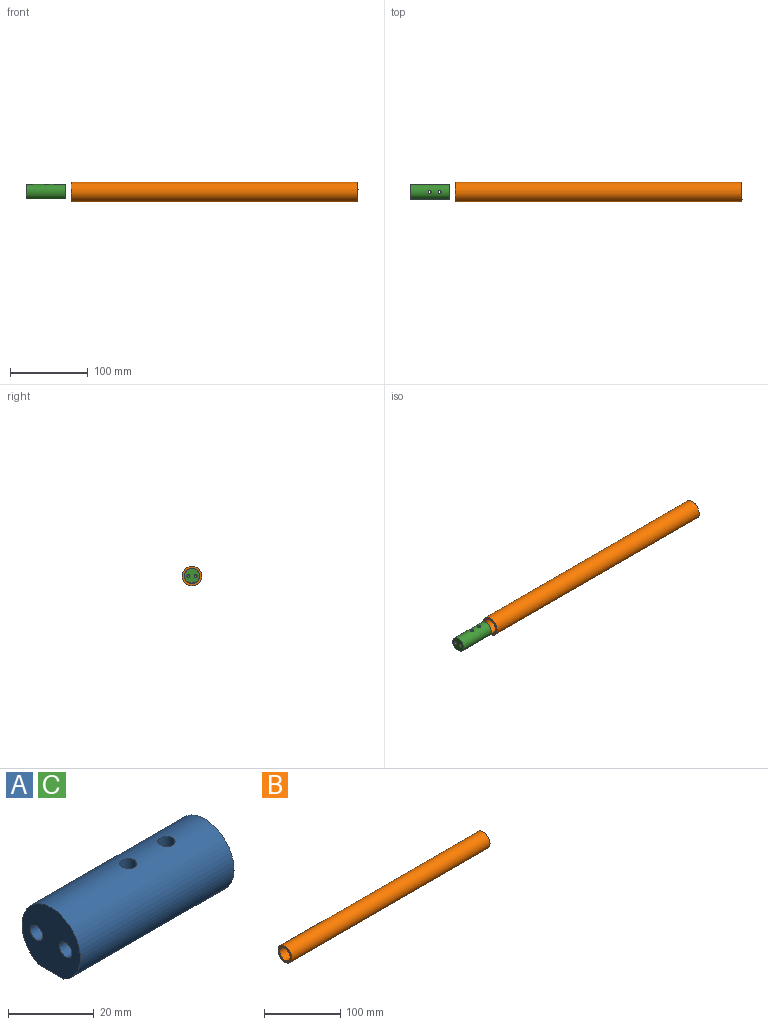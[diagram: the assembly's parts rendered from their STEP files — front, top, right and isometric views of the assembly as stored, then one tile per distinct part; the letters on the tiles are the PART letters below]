
ASSEMBLY  parts=3 mates=4
PART A: 10 faces, bbox 50.8x19.3x18.3 mm
  f0: cylinder r=9.65mm len=50.8mm, axis (-1,0,0), area 2612mm2, adj f1,f2,f3,f8,f9
  f1: plane 50.8x8.43mm, normal (0,0,-1), area 402.6mm2, adj f0,f2,f3,f8,f9
  f2: plane 19.3x18.34mm, normal (1,0,0), area 287.2mm2, adj f0,f1
  f3: plane 19.3x18.34mm, normal (-1,0,0), area 261.6mm2, adj f0,f1,f5,f7
  f4: cone r=0mm half-angle=59deg, axis (-1,0,0), area 14.9mm2, adj f5
  f5: cylinder r=2.02mm len=15.08mm, axis (-1,0,0), area 191.3mm2, adj f3,f4
  f6: cone r=0mm half-angle=59deg, axis (-1,0,0), area 14.9mm2, adj f7
  f7: cylinder r=2.02mm len=15.08mm, axis (-1,0,0), area 191.3mm2, adj f3,f6
  f8: cylinder r=2.02mm len=18.34mm, axis (0,0,-1), area 231.3mm2, adj f0,f1
  f9: cylinder r=2.02mm len=18.34mm, axis (0,0,-1), area 231.3mm2, adj f0,f1
PART B: 8 faces, bbox 368.3x25.4x25.4 mm
  f0: cylinder r=12.7mm len=368.3mm, axis (-1,0,0), area 29355.5mm2, adj f2,f3,f4,f5,f6,f7
  f1: cylinder r=9.65mm len=368.3mm, axis (-1,0,0), area 22302.3mm2, adj f2,f3,f4,f5,f6,f7
  f2: plane 25.4x25.4mm, normal (1,0,0), area 214mm2, adj f0,f1
  f3: plane 25.4x25.4mm, normal (-1,0,0), area 214mm2, adj f0,f1
  f4: cylinder r=1.63mm len=3.26mm, axis (0,0,1), area 31.4mm2, adj f0,f1
  f5: cylinder r=1.63mm len=3.26mm, axis (0,0,1), area 31.4mm2, adj f0,f1
  f6: cylinder r=1.63mm len=3.26mm, axis (0,0,1), area 31.4mm2, adj f0,f1
  f7: cylinder r=1.63mm len=3.26mm, axis (0,0,1), area 31.4mm2, adj f0,f1
PART C: same geometry as A
PLACE A rot(axis=(0,0,-1),180deg) t=(172.38,-129.64,-131.28)mm
PLACE B rot(axis=(-0.08,0.37,0.93),0deg) t=(12.43,-129.64,-131.28)mm
PLACE C rot(axis=(-0.08,0.37,0.93),0deg) t=(-204.55,-129.64,-131.28)mm
MATE parallel C.f0 <-> B.f1  axis (-1,0,0) through (-229.95,-129.64,-131.28)mm
MATE parallel A.f0 <-> B.f1  axis (1,0,0) through (197.78,-129.64,-131.28)mm
MATE slider C.f0 <-> B.f1  axis (1,0,0) through (-179.15,-129.64,-131.28)mm
MATE slider A.f0 <-> B.f0  axis (1,0,0) through (146.98,-129.64,-131.28)mm
